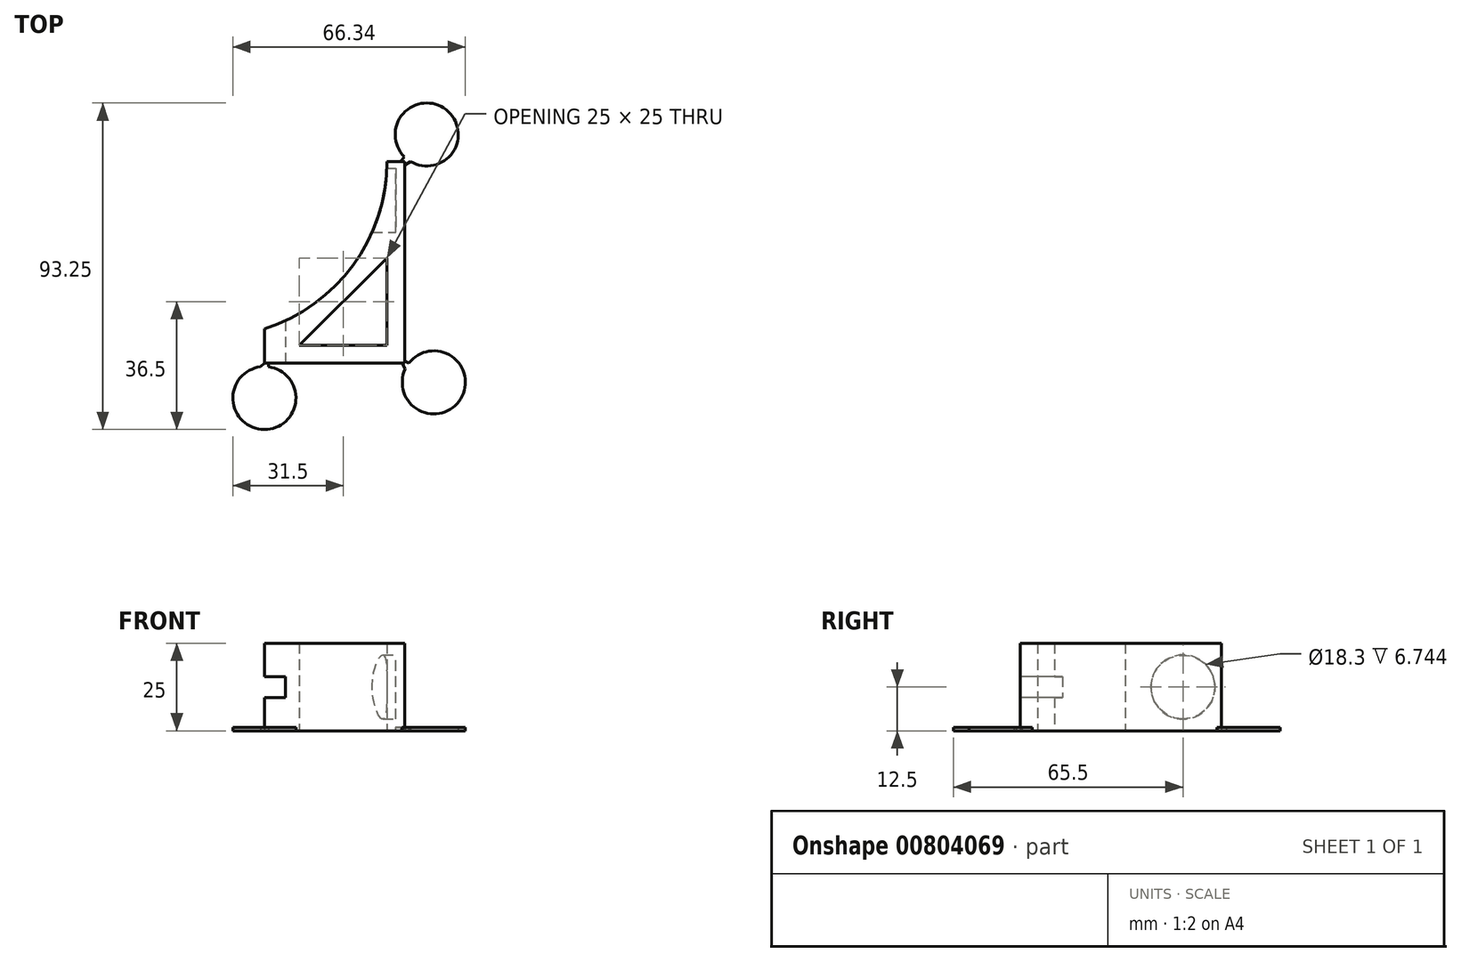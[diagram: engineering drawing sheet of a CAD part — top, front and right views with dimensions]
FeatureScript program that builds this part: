
annotation { "Feature Type Name" : "Feature", "Feature Type Description" : "" }
export const myFeature = defineFeature(function(context is Context, id is Id, definition is map)
    precondition{}
    {
        {
            var Q0;
            Q0=qCreatedBy(makeId("Top.planeOp"),FACE);
            var sketch = newSketch(context, id + "F0", { "sketchPlane" : qUnion([Q0])});
            skArc(sketch, "E0", {"start": v(-50, 0) * mm, "mid": v(0, -50) * mm, "end": v(50, 0) * mm});
            skArc(sketch, "E1", {"start": v(-55, 0) * mm, "mid": v(0, -55) * mm, "end": v(55, 0) * mm});
            skLineSegment(sketch, "E2", {"start": v(-55, 0) * mm, "end": v(-50, 0) * mm});
            skLineSegment(sketch, "E3.trimOffspring", {"start": v(50, 0) * mm, "end": v(55, 0) * mm});
            skSolve(sketch);
        }
        {
            var Q0;
            Q0=qSketchRegion(id+"F0",true);
            extrude(context, id + "F1", {"entities" : qUnion([Q0]), "endBound" : BoundingType.SYMMETRIC, "depth" : 25 * mm, "offsetDistance" : 25 * mm});
        }
        {
            var Q0;
            Q0=makeQuery(id+"F1.opExtrude","CAP_FACE",FACE,{"disambiguationData":[OSD([sQuery(id+"F0.wireOp",EDGE,"E0"),sQuery(id+"F0.wireOp",EDGE,"E1")])],"isStart":false});
            var sketch = newSketch(context, id + "F2", { "sketchPlane" : qUnion([Q0])});
            skLineSegment(sketch, "E4", {"start": v(-55, 0) * mm, "end": v(-55, -57.5) * mm});
            skLineSegment(sketch, "E5", {"start": v(55, 0) * mm, "end": v(55, -57.5) * mm});
            skLineSegment(sketch, "E6", {"start": v(0, -57.5) * mm, "end": v(55, -57.5) * mm});
            skLineSegment(sketch, "E7", {"start": v(0, -57.5) * mm, "end": v(-55, -57.5) * mm});
            skArc(sketch, "E8", {"start": v(-55, 0) * mm, "mid": v(0, -55) * mm, "end": v(55, 0) * mm});
            skLineSegment(sketch, "E9", {"start": v(0, -55) * mm, "end": v(0, -57.5) * mm, "construction": true});
            skSolve(sketch);
        }
        {
            var Q0;
            Q0=qSketchRegion(id+"F2",true);
            extrude(context, id + "F3", {"entities" : qUnion([Q0]), "operationType" : NewBodyOperationType.ADD, "oppositeDirection" : true, "depth" : 25 * mm, "offsetDistance" : 25 * mm});
        }
        {
            var Q0;
            Q0=qCreatedBy(makeId("Front.planeOp"),FACE);
            var sketch = newSketch(context, id + "F4", { "sketchPlane" : qUnion([Q0])});
            skCircle(sketch, "E10", {"center": v(0, 0) * mm, "radius": 9.05 * mm});
            skSolve(sketch);
        }
        {
            var Q0;
            Q0=qSketchRegion(id+"F4",true);
            extrude(context, id + "F5", {"entities" : qUnion([Q0]), "operationType" : NewBodyOperationType.REMOVE, "depth" : 55 * mm, "offsetDistance" : 25 * mm});
        }
        {
            var Q0;
            Q0=qCreatedBy(makeId("Right.planeOp"),FACE);
            var sketch = newSketch(context, id + "F6", { "sketchPlane" : qUnion([Q0])});
            skLineSegment(sketch, "E11", {"start": v(0, 0) * mm, "end": v(-11, 0) * mm, "construction": true});
            skCircle(sketch, "E12", {"center": v(-11, 0) * mm, "radius": 9.15 * mm});
            skSolve(sketch);
        }
        {
            var Q0;
            Q0=qSketchRegion(id+"F6",true);
            extrude(context, id + "F7", {"entities" : qUnion([Q0]), "operationType" : NewBodyOperationType.REMOVE, "endBound" : BoundingType.SYMMETRIC, "oppositeDirection" : true, "depth" : 105 * mm, "offsetDistance" : 25 * mm});
        }
        {
            var Q0;
            Q0=makeQuery(id+"Fw2s3fRRbLm751U_1.boolean.opBoolean","MERGE",FACE,{"derivedFrom":[makeQuery(id+"F3.opExtrude","SWEPT_FACE",FACE,{"disambiguationData":[OSD([sQuery(id+"F2.wireOp",EDGE,"E6"),sQuery(id+"F2.wireOp",EDGE,"E7")])]}),makeQuery(id+"Fw2s3fRRbLm751U_1.opExtrude","CAP_FACE",FACE,{"disambiguationData":[OSD([sQuery(id+"FbaxaLrkKh4OAbq_1.wireOp",EDGE,"Uh6Jvepg-wHhE-7TOv-bsKJ-5smjprHOjM1U"),sQuery(id+"FbaxaLrkKh4OAbq_1.wireOp",EDGE,"EqKOSp2a-ZZTN-DRED-kn9J-UNl89jEZ64Ds"),sQuery(id+"FbaxaLrkKh4OAbq_1.wireOp",EDGE,"ZmvICauE-ycvL-Liv1-Rvg1-fR7zCyWJYo9d"),sQuery(id+"FbaxaLrkKh4OAbq_1.wireOp",EDGE,"3XJykIYq-c0Fd-PVl1-zVKK-2PRkdqiL36qN")])],"isStart":true}),makeQuery(id+"Fw2s3fRRbLm751U_1.opExtrude","CAP_FACE",FACE,{"disambiguationData":[OSD([sQuery(id+"FbaxaLrkKh4OAbq_1.wireOp",EDGE,"GsqChSM5-zfp9-9awz-fXtX-bcvzSKGByjCJ"),sQuery(id+"FbaxaLrkKh4OAbq_1.wireOp",EDGE,"TJYVOPY7-KdYb-aWGS-gSH3-bccdZTbLIemp"),sQuery(id+"FbaxaLrkKh4OAbq_1.wireOp",EDGE,"y8iyoKja-MJTQ-VVae-WmUz-OmJ1Lh6F321q"),sQuery(id+"FbaxaLrkKh4OAbq_1.wireOp",EDGE,"VjoY1uHj-MWVZ-gvii-hLuD-O1X8sx4YcAj0")])],"isStart":true}),makeQuery(id+"Fw2s3fRRbLm751U_1.opExtrude","CAP_FACE",FACE,{"disambiguationData":[OSD([sQuery(id+"FbaxaLrkKh4OAbq_1.wireOp",EDGE,"LKfXc4Wq-0Dhk-OaNw-otnj-FMiGwPJYywq5"),sQuery(id+"FbaxaLrkKh4OAbq_1.wireOp",EDGE,"D16J0ZAf-aM8n-095F-KM0Z-FLc2XpjwKHqT"),sQuery(id+"FbaxaLrkKh4OAbq_1.wireOp",EDGE,"lry7SeKh-0dhK-NucU-Ig3d-D6Hq78D69W9Q"),sQuery(id+"FbaxaLrkKh4OAbq_1.wireOp",EDGE,"Dx4dImNw-9Hc8-QJXM-hLEA-z2wreAxsL18m")])],"isStart":true}),makeQuery(id+"Fw2s3fRRbLm751U_1.opExtrude","CAP_FACE",FACE,{"disambiguationData":[OSD([sQuery(id+"FbaxaLrkKh4OAbq_1.wireOp",EDGE,"366HpSXE-hHsC-ICny-dxCG-DQL75YAk4dYj"),sQuery(id+"FbaxaLrkKh4OAbq_1.wireOp",EDGE,"3hgmhh0g-2aHh-65Z7-dpIf-xj2OcLCkW44q"),sQuery(id+"FbaxaLrkKh4OAbq_1.wireOp",EDGE,"GztjvuJG-5ALz-OUHu-07ZH-pbl2oPdiQVm3"),sQuery(id+"FbaxaLrkKh4OAbq_1.wireOp",EDGE,"92lCGce6-pG3P-tAXz-iT5i-Sx4S5zZef9y7")])],"isStart":true}),makeQuery(id+"Fw2s3fRRbLm751U_1.opExtrude","CAP_FACE",FACE,{"disambiguationData":[OSD([sQuery(id+"FbaxaLrkKh4OAbq_1.wireOp",EDGE,"KpZNk49n-1Lbj-VffG-t7Zu-HfJjVrSZoJnn"),sQuery(id+"FbaxaLrkKh4OAbq_1.wireOp",EDGE,"GRcNCLOO-jY07-0M9A-xyGv-PHShYkRzWhOY"),sQuery(id+"FbaxaLrkKh4OAbq_1.wireOp",EDGE,"7gz4Tj37-H0f3-I8EB-FIRw-Ged3O8sxXS7n"),sQuery(id+"FbaxaLrkKh4OAbq_1.wireOp",EDGE,"uc3IzkU7-TclG-YgYZ-q9s7-G10LoXP5muE5")])],"isStart":true}),makeQuery(id+"Fw2s3fRRbLm751U_1.opExtrude","CAP_FACE",FACE,{"disambiguationData":[OSD([sQuery(id+"FbaxaLrkKh4OAbq_1.wireOp",EDGE,"cPWaBmpP-2oLx-1DeM-AJb3-IhrFnr4dnm24"),sQuery(id+"FbaxaLrkKh4OAbq_1.wireOp",EDGE,"8OEXvs0X-7gBm-KFCK-AZCW-AgfPs4lSShVE"),sQuery(id+"FbaxaLrkKh4OAbq_1.wireOp",EDGE,"Tr4TIrwc-Pu5s-xqs2-cugA-VtfyKg5LKPk4"),sQuery(id+"FbaxaLrkKh4OAbq_1.wireOp",EDGE,"GVU8kKog-5Xpu-DsKy-gFNO-yMKygH5Buhjr")])],"isStart":true})]});
            var sketch = newSketch(context, id + "F8", { "sketchPlane" : qUnion([Q0])});
            skLineSegment(sketch, "E13", {"start": v(0, 12.5) * mm, "end": v(0, -12.5) * mm, "construction": true});
            skLineSegment(sketch, "E14.bottom", {"start": v(-15, 12.5) * mm, "end": v(15, 12.5) * mm});
            skLineSegment(sketch, "E14.top", {"start": v(-15, -12.5) * mm, "end": v(15, -12.5) * mm});
            skLineSegment(sketch, "E14.right", {"start": v(15, 12.5) * mm, "end": v(15, 3) * mm});
            skLineSegment(sketch, "E15", {"start": v(15, 0) * mm, "end": v(0, 0) * mm, "construction": true});
            skLineSegment(sketch, "E16", {"start": v(0, 0) * mm, "end": v(-15, 0) * mm, "construction": true});
            skLineSegment(sketch, "E17", {"start": v(15, 0) * mm, "end": v(21, 0) * mm, "construction": true});
            skLineSegment(sketch, "E18", {"start": v(21, 0) * mm, "end": v(21, 3) * mm});
            skLineSegment(sketch, "E19", {"start": v(21, 3) * mm, "end": v(15, 3) * mm});
            skLineSegment(sketch, "E20", {"start": v(21, 0) * mm, "end": v(21, -3) * mm});
            skLineSegment(sketch, "E21", {"start": v(21, -3) * mm, "end": v(15, -3) * mm});
            skLineSegment(sketch, "E22.trimOffspring", {"start": v(15, -3) * mm, "end": v(15, -12.5) * mm});
            skLineSegment(sketch, "E23", {"start": v(-15, 12.5) * mm, "end": v(-15, 48.38) * mm});
            skLineSegment(sketch, "E24", {"start": v(-15, 48.38) * mm, "end": v(-89.99, 48.38) * mm});
            skLineSegment(sketch, "E25", {"start": v(-89.99, 48.38) * mm, "end": v(-91.23, -54.8) * mm});
            skLineSegment(sketch, "E26", {"start": v(-91.23, -54.8) * mm, "end": v(-15, -56.86) * mm});
            skLineSegment(sketch, "E27", {"start": v(-15, -56.86) * mm, "end": v(-15, -12.5) * mm});
            skSolve(sketch);
        }
        {
            var Q0;
            Q0 = qSketchRegion(id + "F8", true);
            extrude(context, id + "F9", {"entities" : qUnion([Q0]), "operationType" : NewBodyOperationType.REMOVE, "endBound" : BoundingType.THROUGH_ALL, "oppositeDirection" : true, "depth" : 25 * mm, "offsetDistance" : 25 * mm});
        }
        {
            var Q0;
            Q0=makeQuery(id+"F3.boolean.opBoolean","MERGE",FACE,{"derivedFrom":[makeQuery(id+"F1.opExtrude","CAP_FACE",FACE,{"disambiguationData":[OSD([sQuery(id+"F0.wireOp",EDGE,"E0"),sQuery(id+"F0.wireOp",EDGE,"E1"),sQuery(id+"F0.wireOp",EDGE,"E2"),sQuery(id+"F0.wireOp",EDGE,"E3.trimOffspring")])],"isStart":true}),makeQuery(id+"F3.opExtrude","CAP_FACE",FACE,{"disambiguationData":[OSD([sQuery(id+"F2.wireOp",EDGE,"E4"),sQuery(id+"F2.wireOp",EDGE,"E5"),sQuery(id+"F2.wireOp",EDGE,"E6"),sQuery(id+"F2.wireOp",EDGE,"E7"),sQuery(id+"F2.wireOp",EDGE,"E8")])],"isStart":false})]});
            var sketch = newSketch(context, id + "F10", { "sketchPlane" : qUnion([Q0])});
            skLineSegment(sketch, "E28.1", {"start": v(50, 52.5) * mm, "end": v(25, 52.5) * mm});
            skLineSegment(sketch, "E28.2", {"start": v(50, 27.5) * mm, "end": v(50, 52.5) * mm});
            skLineSegment(sketch, "E29", {"start": v(25, 52.5) * mm, "end": v(50, 27.5) * mm});
            skSolve(sketch);
        }
        {
            var Q0;
            Q0 = qSketchRegion(id + "F10", true);
            extrude(context, id + "F11", {"entities" : qUnion([Q0]), "operationType" : NewBodyOperationType.REMOVE, "oppositeDirection" : true, "depth" : 25 * mm, "offsetDistance" : 25 * mm});
        }
        {
            var Q0;
            Q0=makeQuery(id+"F3.boolean.opBoolean","MERGE",FACE,{"derivedFrom":[makeQuery(id+"F1.opExtrude","CAP_FACE",FACE,{"disambiguationData":[OSD([sQuery(id+"F0.wireOp",EDGE,"E0"),sQuery(id+"F0.wireOp",EDGE,"E1"),sQuery(id+"F0.wireOp",EDGE,"E2"),sQuery(id+"F0.wireOp",EDGE,"E3.trimOffspring")])],"isStart":true}),makeQuery(id+"F3.opExtrude","CAP_FACE",FACE,{"disambiguationData":[OSD([sQuery(id+"F2.wireOp",EDGE,"E4"),sQuery(id+"F2.wireOp",EDGE,"E5"),sQuery(id+"F2.wireOp",EDGE,"E6"),sQuery(id+"F2.wireOp",EDGE,"E7"),sQuery(id+"F2.wireOp",EDGE,"E8")])],"isStart":false})]});
            var sketch = newSketch(context, id + "F12", { "sketchPlane" : qUnion([Q0])});
            skLineSegment(sketch, "E30", {"start": v(15, 57.5) * mm, "end": v(15, 67.5) * mm, "construction": true});
            skLineSegment(sketch, "E31", {"start": v(55, 0) * mm, "end": v(61.32, -7.75) * mm, "construction": true});
            skLineSegment(sketch, "E32", {"start": v(55, 57.5) * mm, "end": v(63.34, 63.02) * mm, "construction": true});
            skArc(sketch, "E33", {"start": v(16.2, 58.58) * mm, "mid": v(14.94, 76.5) * mm, "end": v(13.92, 58.56) * mm});
            skArc(sketch, "E34", {"start": v(56.23, 57.5) * mm, "mid": v(71.02, 67.7) * mm, "end": v(55.18, 59.23) * mm});
            skArc(sketch, "E35", {"start": v(54.92, -1.42) * mm, "mid": v(66.87, -14.84) * mm, "end": v(56.74, 0) * mm});
            skLineSegment(sketch, "E36", {"start": v(56.74, 0) * mm, "end": v(55, 1.02) * mm});
            skLineSegment(sketch, "E37", {"start": v(53.94, 0) * mm, "end": v(54.92, -1.42) * mm});
            skLineSegment(sketch, "E38", {"start": v(53.94, 0) * mm, "end": v(55, 0) * mm});
            skLineSegment(sketch, "E39", {"start": v(55, 1.02) * mm, "end": v(55, 0) * mm});
            skLineSegment(sketch, "E40", {"start": v(55.18, 59.23) * mm, "end": v(54.3, 57.5) * mm});
            skLineSegment(sketch, "E41", {"start": v(54.3, 57.5) * mm, "end": v(55, 57.5) * mm});
            skLineSegment(sketch, "E42", {"start": v(56.23, 57.5) * mm, "end": v(55, 56.88) * mm});
            skLineSegment(sketch, "E43", {"start": v(55, 56.88) * mm, "end": v(55, 57.5) * mm});
            skLineSegment(sketch, "E44", {"start": v(16.2, 58.58) * mm, "end": v(16.2, 57.5) * mm});
            skLineSegment(sketch, "E45", {"start": v(16.2, 57.5) * mm, "end": v(15, 57.5) * mm});
            skLineSegment(sketch, "E46", {"start": v(13.92, 58.56) * mm, "end": v(15, 57.5) * mm});
            skSolve(sketch);
        }
        {
            var Q0;
            Q0 = qSketchRegion(id + "F12", true);
            extrude(context, id + "F13", {"entities" : qUnion([Q0]), "operationType" : NewBodyOperationType.ADD, "oppositeDirection" : true, "depth" : 1 * mm, "offsetDistance" : 25 * mm});
        }
    });
